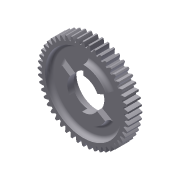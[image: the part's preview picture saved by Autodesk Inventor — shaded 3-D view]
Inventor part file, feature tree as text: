
AUTODESK INVENTOR PART (.ipt)
format: ipt  version: 2011 (Build 150239000, 239)  size: 414,720 bytes
history: native  units: mm (DEFAULTED — no unit token found)
features: sketch x6, other x4, extrude x4, plane x3, fillet x2, revolve x1, pattern_circular x1, projected_geometry x1
ambient origin geometry x8: Origin, YZ Plane, XZ Plane, XY Plane, X Axis, Y Axis, Z Axis, Center Point
bodies: Solid1 (feature_tree)
feature tree (22):
  other  "Gear 48T dog shift"
  extrude  "Extrusion1"  Depth=9.525mm TaperAngle=0.0deg
  plane  "Work Plane1"
  plane  "Work Plane2"
  plane  "Work Plane3"
  other  "Spur Gear"
  extrude  "Extrusion4"  Depth=76.2mm TaperAngle=0.0deg
  extrude  "Extrusion6"  TaperAngle=0.0deg  [1 undecoded]
  revolve  "Revolution3"  [1 undecoded]
  fillet  "Fillet1"  Radius=28.575mm
  extrude  "Extrusion7"  Depth=53.975mm
  pattern_circular  "Circular Pattern1"  [2 undecoded]
  fillet  "Fillet2"  Radius=3.6576mm
  sketch  "Sketch1"  dims[d0=63.5mm d1=9.525mm d2=0.0mm]
  sketch  "Sketch2"  dims[d3=60.96mm d4=76.2mm d5=0.0mm]
  other  "Srf1"
  sketch  "Sketch6"  dims[d6=0.0mm d7=0.654498mm d9=0.0mm]
  sketch  "Sketch7"  dims[d14=0.0mm d15=152.4mm d16=0.0mm]
  sketch  "Sketch8"  dims[d17=0.0mm d18=0.0mm d19=152.4mm d31=28.575mm]
  sketch  "Sketch9"  dims[d32=5.08mm d33=0.0mm d34=53.975mm d37=22.225mm d38=3.6576mm d39=0.0mm d45=17.78mm d47=5.08mm d48=3.6576mm d49=90.0deg d50=2.54mm d51=9.773844mm d52=3.6576mm d53=0.0mm d54=30.0mm d55=360.0deg d57=2.54mm]
  other  "Pitch Diameter"
  projected_geometry  "Project Cut Edges2"
note: 4 required parameter values undecoded (feature->parameter linkage not recoverable at this tier; creation-order binding heuristic only, values carry confidence <= 0.55)